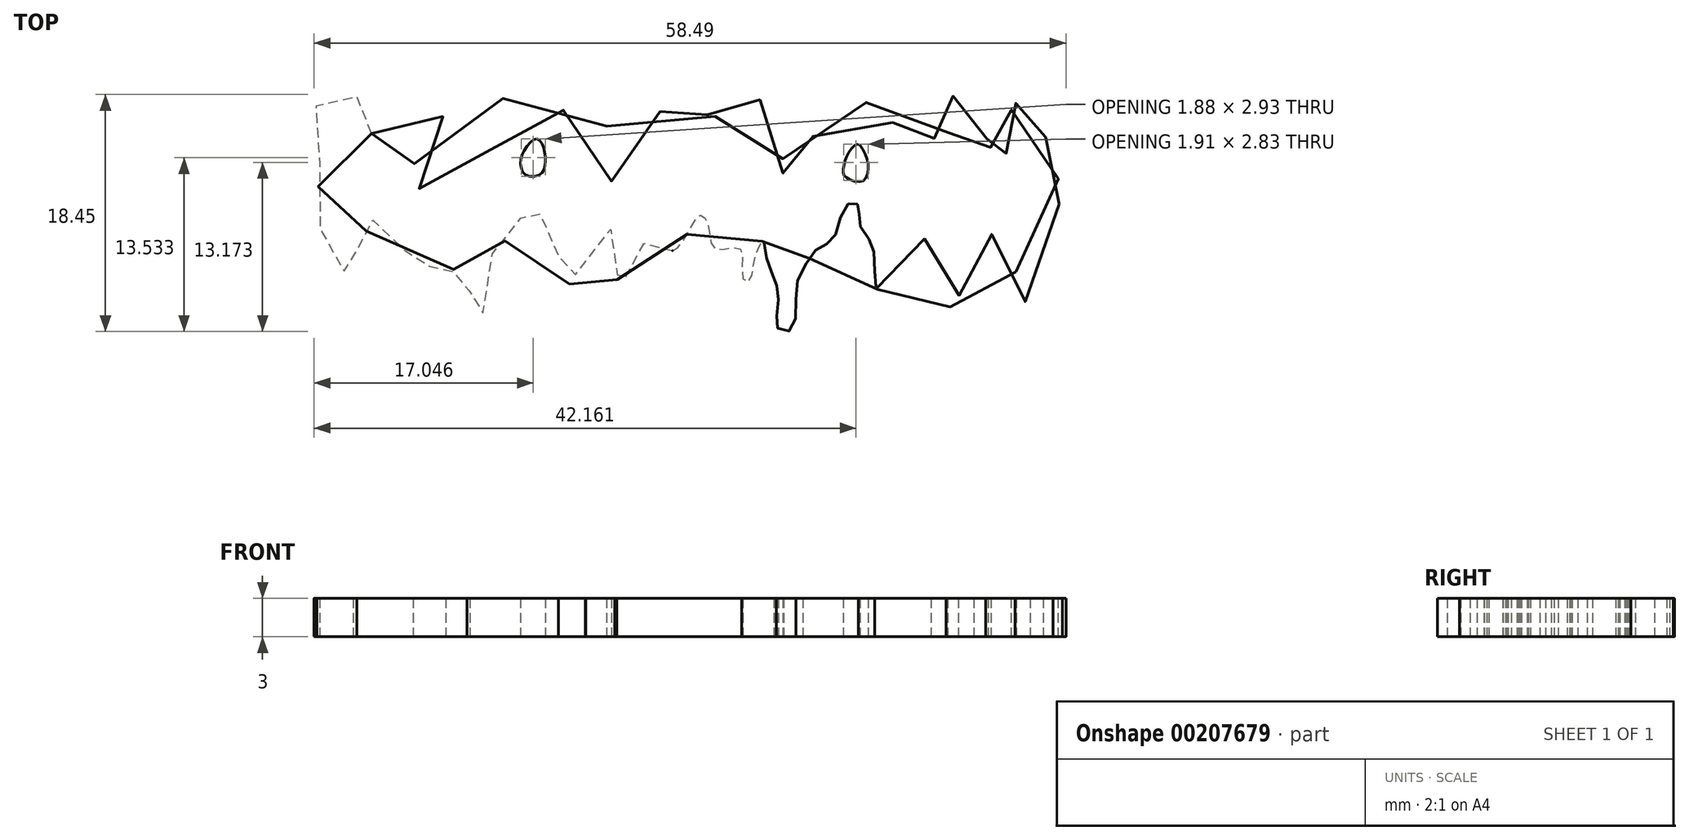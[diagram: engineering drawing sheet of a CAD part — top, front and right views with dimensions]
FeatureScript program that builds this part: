
annotation { "Feature Type Name" : "Feature", "Feature Type Description" : "" }
export const myFeature = defineFeature(function(context is Context, id is Id, definition is map)
    precondition{}
    {
        {
            var Q0;
            Q0=qCreatedBy(makeId("Top.planeOp"),FACE);
            var sketch = newSketch(context, id + "F0", { "sketchPlane" : qUnion([Q0])});
            skFitSpline(sketch, "E0", {"points": [v(-24.82, 4.4) * mm, v(-25.27, 4.74) * mm, v(-25.4, 5.94) * mm, v(-25.6, 6.87) * mm, v(-25.95, 7.25) * mm, v(-27.12, 7.38) * mm, v(-28.42, 7.21) * mm, v(-28.87, 6.87) * mm, v(-29.24, 6.36) * mm, v(-29.18, 5.05) * mm, v(-28.9, 2.96) * mm, v(-28.9, 1.25) * mm, v(-29.07, -1.3) * mm, v(-28.83, -3) * mm, v(-28.11, -3.7) * mm, v(-27.26, -4.2) * mm, v(-26.98, -5.99) * mm, v(-26.7, -7.3) * mm, v(-26.23, -7.3) * mm, v(-25.99, -6.37) * mm, v(-26.26, -4.69) * mm, v(-26.02, -4.07) * mm, v(-25.47, -3.49) * mm, v(-24.92, -2.63) * mm, v(-24.51, -2.18) * mm, v(-23.65, -2.35) * mm, v(-22.83, -3.45) * mm, v(-22.15, -4.93) * mm, v(-21.97, -5.61) * mm, v(-21.63, -5.68) * mm, v(-21.22, -5.27) * mm, v(-20.57, -5.85) * mm, v(-19.57, -5.95) * mm, v(-19.44, -6.64) * mm, v(-19.2, -6.98) * mm, v(-18.82, -6.85) * mm, v(-18.4, -6.02) * mm, v(-18.27, -5.65) * mm, v(-17.76, -6.16) * mm, v(-17.17, -7.36) * mm, v(-17.31, -8.15) * mm, v(-17.2, -10.04) * mm, v(-16.56, -10.2) * mm, v(-16.21, -9.8) * mm, v(-16.11, -8.84) * mm, v(-15.94, -6.4) * mm, v(-15.46, -5.06) * mm, v(-14.8, -4.07) * mm, v(-13.98, -3.83) * mm, v(-13.5, -3.07) * mm, v(-12.85, -1.15) * mm, v(-12.44, -0.57) * mm, v(-12.1, -0.6) * mm, v(-11.8, -1.36) * mm, v(-11.52, -2.56) * mm, v(-10.86, -3.42) * mm, v(-10.35, -4.1) * mm, v(-10.28, -5.37) * mm, v(-9.97, -6.68) * mm, v(-9.7, -7.33) * mm, v(-9.18, -7.12) * mm, v(-8.88, -6.1) * mm, v(-8.7, -5.4) * mm, v(-8.46, -4.82) * mm, v(-8.19, -4.93) * mm, v(-8.16, -5.2) * mm, v(-7.7, -5.2) * mm, v(-7.1, -4.27) * mm, v(-6.78, -3.66) * mm, v(-6.61, -3.52) * mm, v(-6.3, -3.07) * mm, v(-6, -3.21) * mm, v(-5.9, -4.48) * mm, v(-5.75, -5.75) * mm, v(-5.72, -6.78) * mm, v(-5.65, -8.12) * mm, v(-5.3, -8.46) * mm, v(-5.14, -7.43) * mm, v(-4.83, -5.58) * mm, v(-4.49, -4.62) * mm, v(-4.18, -4.07) * mm, v(-3.73, -4.07) * mm, v(-3.25, -4.48) * mm, v(-2.33, -4.41) * mm, v(-1.81, -4.03) * mm, v(-1.5, -4.45) * mm, v(-1.4, -4.72) * mm, v(-0.65, -4.03) * mm, v(0.38, -2.29) * mm, v(0.86, -1.94) * mm, v(1.34, -2.66) * mm, v(1.55, -3.97) * mm, v(1.96, -4.58) * mm, v(3.44, -4.48) * mm, v(4.02, -4.82) * mm, v(4.05, -6.85) * mm, v(4.53, -7.12) * mm, v(4.9, -5.71) * mm, v(5.18, -4.72) * mm, v(5.63, -3.93) * mm, v(5.8, -4.75) * mm, v(6.18, -6.13) * mm, v(6.7, -7.4) * mm, v(6.83, -8.56) * mm, v(6.66, -10.14) * mm, v(6.86, -10.82) * mm, v(7.76, -10.93) * mm, v(8.2, -9.49) * mm, v(8.27, -7.19) * mm, v(9.23, -5.34) * mm, v(10.09, -4.38) * mm, v(10.98, -3.97) * mm, v(11.53, -2.53) * mm, v(12.28, -1.05) * mm, v(12.83, -0.98) * mm, v(13.17, -1.57) * mm, v(13.04, -2.22) * mm, v(13.62, -3.52) * mm, v(14.17, -4.38) * mm, v(14.3, -6.4) * mm, v(14.51, -7.67) * mm, v(15.1, -7.88) * mm, v(15.78, -6.37) * mm, v(16.05, -5.5) * mm, v(16.6, -5.65) * mm, v(17.36, -5.17) * mm, v(17.67, -4.2) * mm, v(18.11, -3.76) * mm, v(18.7, -4.41) * mm, v(19.17, -4.65) * mm, v(19.9, -4.75) * mm, v(19.93, -5.92) * mm, v(20.2, -9.08) * mm, v(20.58, -9.1) * mm, v(21.06, -7.3) * mm, v(21.78, -5.3) * mm, v(22.36, -4.9) * mm, v(22.88, -4.65) * mm, v(22.95, -3.8) * mm, v(23.08, -2.6) * mm, v(23.36, -3.07) * mm, v(23.67, -4.17) * mm, v(24.56, -4.65) * mm, v(25.18, -4.93) * mm, v(25.28, -6.74) * mm, v(25.42, -9.21) * mm, v(25.69, -9.25) * mm, v(26.2, -8.12) * mm, v(26.65, -6.1) * mm, v(27.27, -5.06) * mm, v(28.06, -4.93) * mm, v(28.2, -4.17) * mm, v(28.5, -1.63) * mm, v(28.91, 0) * mm, v(28.57, 0.63) * mm, v(28.88, 1.45) * mm, v(29.19, 4.02) * mm, v(29.05, 3.89) * mm, v(27.5, 3.78) * mm, v(27.5, 4.06) * mm, v(28.36, 4.23) * mm, v(28.95, 4.57) * mm, v(29.15, 5.53) * mm, v(28.7, 6.6) * mm, v(27.58, 7.28) * mm, v(25.86, 7.1) * mm, v(25, 6.36) * mm, v(25.04, 5.33) * mm, v(25.76, 4.23) * mm, v(26.4, 3.89) * mm, v(26.34, 3.72) * mm, v(25.14, 3.85) * mm, v(24.76, 3.89) * mm, v(24.56, 2.93) * mm, v(23.94, 0) * mm, v(23.6, -0.6) * mm, v(22.98, -0.67) * mm, v(23.19, 0.83) * mm, v(23.22, 3.96) * mm, v(22.95, 3.96) * mm, v(22.09, 3.89) * mm, v(22.2, 4.26) * mm, v(22.88, 4.74) * mm, v(23.15, 5.64) * mm, v(22.78, 6.63) * mm, v(21.37, 7.18) * mm, v(20.17, 7.32) * mm, v(19.07, 6.87) * mm, v(18.7, 5.9) * mm, v(19.04, 5.02) * mm, v(20.55, 4.26) * mm, v(20.79, 3.96) * mm, v(19.07, 3.99) * mm, v(18.9, 3.99) * mm, v(18.6, 0) * mm, v(18.28, 0) * mm, v(17.53, 0.94) * mm, v(15.95, 4.4) * mm, v(15.64, 5.46) * mm, v(15.03, 6.7) * mm, v(14.34, 6.84) * mm, v(10.8, 6.73) * mm, v(10.26, 6.5) * mm, v(9.92, 5.6) * mm, v(9, 2.3) * mm, v(8, 0) * mm, v(6.73, -1.6) * mm, v(6.49, -1.33) * mm, v(6.9, 0.35) * mm, v(7.24, 1.83) * mm, v(7.2, 2.93) * mm, v(8.27, 4.88) * mm, v(8.72, 5.6) * mm, v(7.79, 6.36) * mm, v(5.56, 7) * mm, v(4.8, 6.97) * mm, v(4.26, 6.18) * mm, v(3.37, 3.96) * mm, v(3.3, 3.72) * mm, v(2.99, 4.6) * mm, v(2.61, 5.4) * mm, v(1.07, 5.88) * mm, v(0.73, 5.7) * mm, v(0, 4.95) * mm, v(-0.61, 3.27) * mm, v(-1.06, 3.06) * mm, v(-1.33, 3.5) * mm, v(-1.85, 5.16) * mm, v(-2.84, 6.66) * mm, v(-3.77, 7.04) * mm, v(-5.82, 6.66) * mm, v(-6.48, 5.9) * mm, v(-6.27, 2.41) * mm, v(-6.27, -0.54) * mm, v(-6.4, -0.6) * mm, v(-7.33, 1.04) * mm, v(-8.43, 3.2) * mm, v(-9.46, 5.09) * mm, v(-9.94, 6.42) * mm, v(-10.38, 7.18) * mm, v(-14.7, 7.1) * mm, v(-14.91, 6.77) * mm, v(-15.73, 4.81) * mm, v(-15.94, 3) * mm, v(-16.93, 0.83) * mm, v(-18.24, -2.05) * mm, v(-18.51, -2.11) * mm, v(-18.96, -1.77) * mm, v(-20.12, -0.98) * mm, v(-21.5, 0.87) * mm, v(-21.43, 2.24) * mm, v(-20.67, 3.1) * mm, v(-20.2, 3.13) * mm, v(-19.57, 2.86) * mm, v(-19.16, 3.3) * mm, v(-19.23, 5.6) * mm, v(-20.26, 7.32) * mm, v(-20.98, 7.42) * mm, v(-22.35, 7.04) * mm, v(-23.28, 6.18) * mm, v(-24.13, 5.64) * mm, v(-24.82, 4.4) * mm]});
            skFitSpline(sketch, "E1", {"points": [v(13, 3.58) * mm, v(12.32, 2.96) * mm, v(11.94, 1.97) * mm, v(11.9, 1.25) * mm, v(12.28, 0.87) * mm, v(13.38, 0.7) * mm, v(13.83, 1.62) * mm, v(13.55, 2.86) * mm, v(13, 3.58) * mm]});
            skFitSpline(sketch, "E2", {"points": [v(-11.96, 3.99) * mm, v(-12.82, 3.3) * mm, v(-13.23, 2.1) * mm, v(-12.82, 1.18) * mm, v(-11.65, 1.25) * mm, v(-11.31, 2.1) * mm, v(-11.45, 3.3) * mm, v(-11.96, 3.99) * mm]});
            skSolve(sketch);
        }
        {
            var Q0;
            Q0 = qSketchRegion(id + "F0", true);
            extrude(context, id + "F1", {"entities" : qUnion([Q0]), "depth" : 3 * mm});
        }
    });
